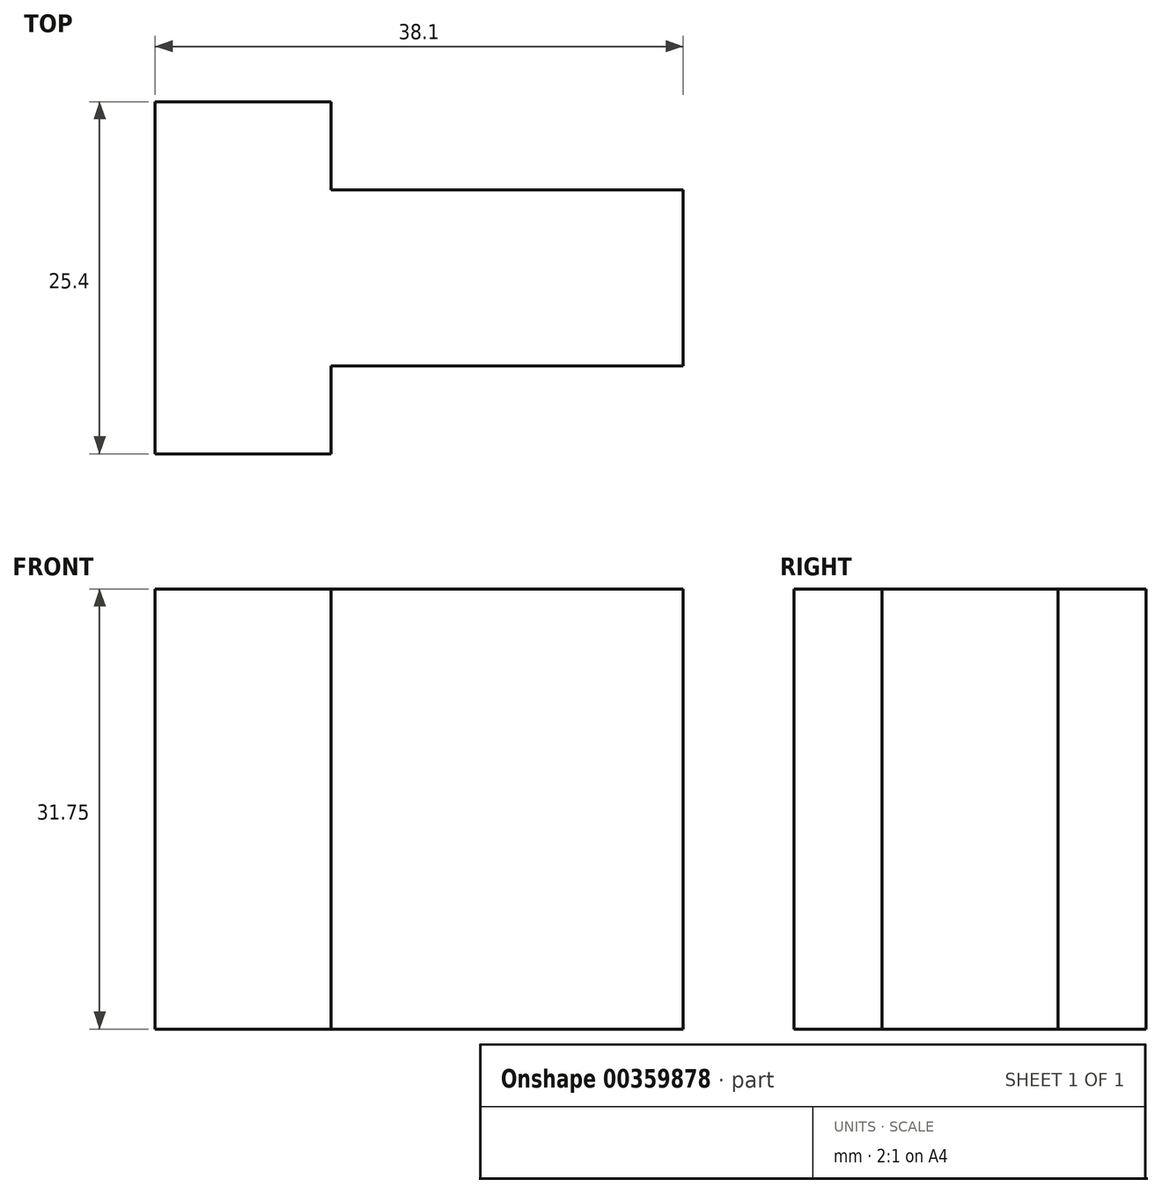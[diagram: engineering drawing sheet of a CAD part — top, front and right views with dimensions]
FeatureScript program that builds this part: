
annotation { "Feature Type Name" : "Feature", "Feature Type Description" : "" }
export const myFeature = defineFeature(function(context is Context, id is Id, definition is map)
    precondition{}
    {
        {
            var Q0;
            Q0=qCreatedBy(makeId("Top.planeOp"),FACE);
            var sketch = newSketch(context, id + "F0", { "sketchPlane" : qUnion([Q0])});
            skLineSegment(sketch, "E0", {"start": v(0, 0) * mm, "end": v(12.7, 0) * mm});
            skLineSegment(sketch, "E1", {"start": v(12.7, 0) * mm, "end": v(12.7, 6.35) * mm});
            skLineSegment(sketch, "E2", {"start": v(12.7, 6.35) * mm, "end": v(38.1, 6.35) * mm});
            skLineSegment(sketch, "E3", {"start": v(38.1, 6.35) * mm, "end": v(38.1, 19.05) * mm});
            skLineSegment(sketch, "E4", {"start": v(38.1, 19.05) * mm, "end": v(12.7, 19.05) * mm});
            skLineSegment(sketch, "E5", {"start": v(12.7, 19.05) * mm, "end": v(12.7, 25.4) * mm});
            skLineSegment(sketch, "E6", {"start": v(12.7, 25.4) * mm, "end": v(0, 25.4) * mm});
            skLineSegment(sketch, "E7", {"start": v(0, 25.4) * mm, "end": v(0, 0) * mm});
            skSolve(sketch);
        }
        {
            var Q0;
            Q0 = qSketchRegion(id + "F0", true);
            extrude(context, id + "F1", {"entities" : qUnion([Q0]), "depth" : 31.75 * mm});
        }
    });
